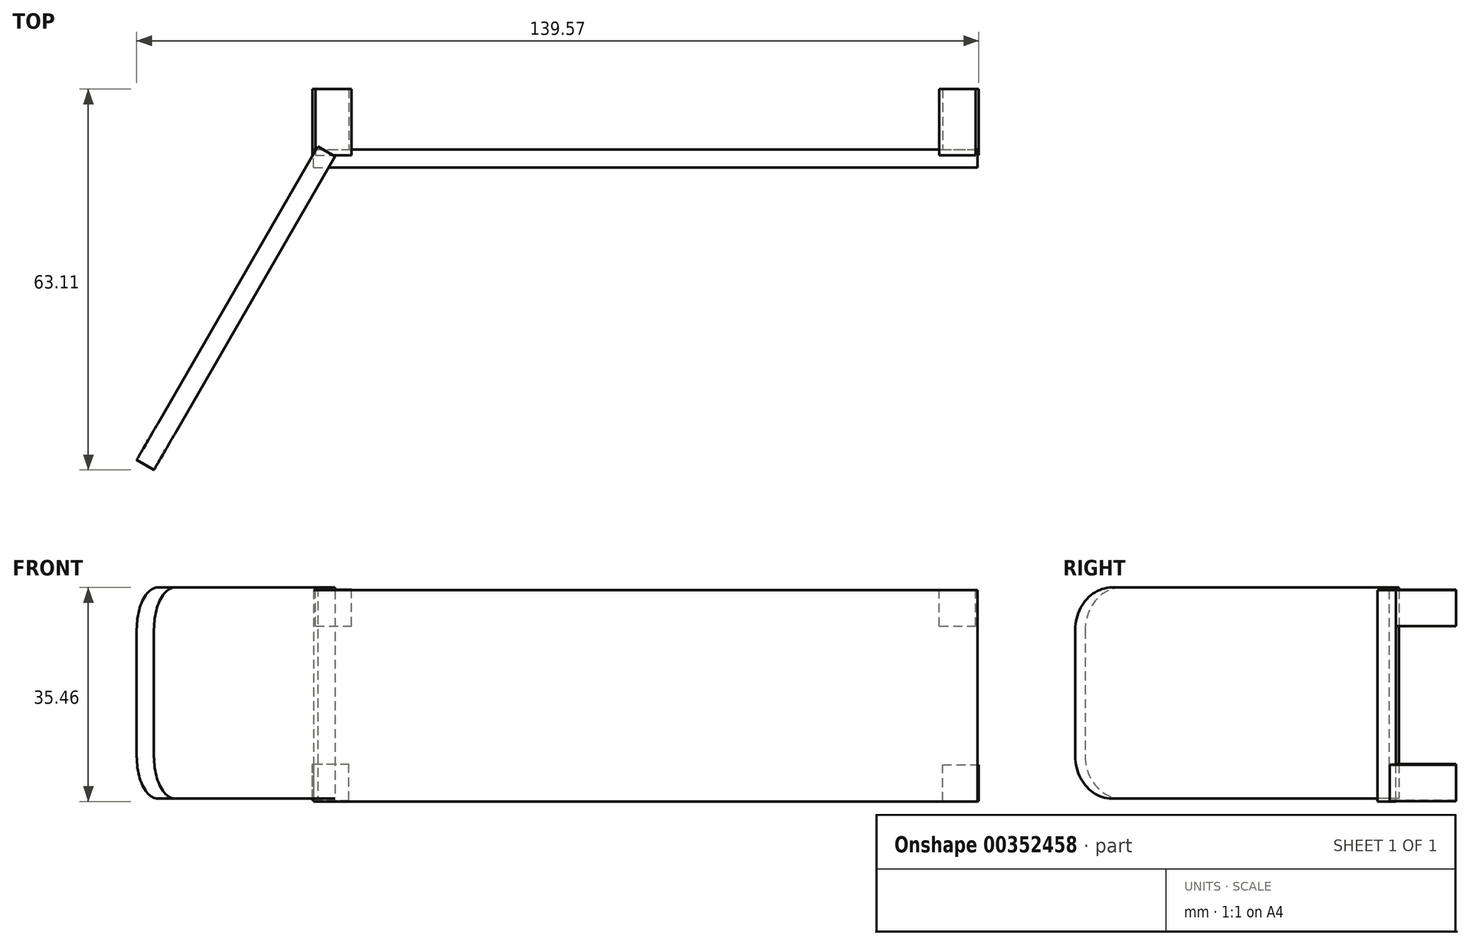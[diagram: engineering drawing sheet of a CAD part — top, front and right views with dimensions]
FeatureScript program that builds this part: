
annotation { "Feature Type Name" : "Feature", "Feature Type Description" : "" }
export const myFeature = defineFeature(function(context is Context, id is Id, definition is map)
    precondition{}
    {
        {
            var Q0;
            Q0=qCreatedBy(makeId("Front.planeOp"),FACE);
            var sketch = newSketch(context, id + "F0", { "sketchPlane" : qUnion([Q0])});
            skLineSegment(sketch, "E0.bottom", {"start": v(-50.03, 27.7) * mm, "end": v(59.97, 27.7) * mm});
            skLineSegment(sketch, "E0.top", {"start": v(-50.03, -7.3) * mm, "end": v(59.97, -7.3) * mm});
            skLineSegment(sketch, "E0.left", {"start": v(-50.03, 27.7) * mm, "end": v(-50.03, -7.3) * mm});
            skLineSegment(sketch, "E0.right", {"start": v(59.97, 27.7) * mm, "end": v(59.97, -7.3) * mm});
            skSolve(sketch);
        }
        {
            var Q0;
            Q0 = qSketchRegion(id + "F0", true);
            extrude(context, id + "F1", {"entities" : qUnion([Q0]), "depth" : 3 * mm});
        }
        {
            var Q0;
            Q0=qCreatedBy(makeId("Front.planeOp"),FACE);
            var sketch = newSketch(context, id + "F2", { "sketchPlane" : qUnion([Q0])});
            skLineSegment(sketch, "E1.bottom", {"start": v(-50.21, -7.14) * mm, "end": v(-44.21, -7.14) * mm});
            skLineSegment(sketch, "E1.top", {"start": v(-50.21, -1.14) * mm, "end": v(-44.21, -1.14) * mm});
            skLineSegment(sketch, "E1.left", {"start": v(-50.21, -7.14) * mm, "end": v(-50.21, -1.14) * mm});
            skLineSegment(sketch, "E1.right", {"start": v(-44.21, -7.14) * mm, "end": v(-44.21, -1.14) * mm});
            skLineSegment(sketch, "E2.bottom", {"start": v(-49.75, 21.78) * mm, "end": v(-43.75, 21.78) * mm});
            skLineSegment(sketch, "E2.top", {"start": v(-49.75, 27.78) * mm, "end": v(-43.75, 27.78) * mm});
            skLineSegment(sketch, "E2.left", {"start": v(-49.75, 21.78) * mm, "end": v(-49.75, 27.78) * mm});
            skLineSegment(sketch, "E2.right", {"start": v(-43.75, 21.78) * mm, "end": v(-43.75, 27.78) * mm});
            skLineSegment(sketch, "E3.bottom", {"start": v(54.2, -7.26) * mm, "end": v(60.2, -7.26) * mm});
            skLineSegment(sketch, "E3.top", {"start": v(54.2, -1.26) * mm, "end": v(60.2, -1.26) * mm});
            skLineSegment(sketch, "E3.left", {"start": v(54.2, -7.26) * mm, "end": v(54.2, -1.26) * mm});
            skLineSegment(sketch, "E3.right", {"start": v(60.2, -7.26) * mm, "end": v(60.2, -1.26) * mm});
            skLineSegment(sketch, "E4.bottom", {"start": v(53.68, 21.72) * mm, "end": v(59.68, 21.72) * mm});
            skLineSegment(sketch, "E4.top", {"start": v(53.68, 27.72) * mm, "end": v(59.68, 27.72) * mm});
            skLineSegment(sketch, "E4.left", {"start": v(53.68, 21.72) * mm, "end": v(53.68, 27.72) * mm});
            skLineSegment(sketch, "E4.right", {"start": v(59.68, 21.72) * mm, "end": v(59.68, 27.72) * mm});
            skSolve(sketch);
        }
        {
            var Q0;
            Q0 = qSketchRegion(id + "F2", true);
            extrude(context, id + "F3", {"entities" : qUnion([Q0]), "operationType" : NewBodyOperationType.ADD, "oppositeDirection" : true, "depth" : 10 * mm, "hasSecondDirection" : true, "secondDirectionOppositeDirection" : false, "secondDirectionDepth" : 1 * mm});
        }
        {
            var Q0;
            Q0=qCreatedBy(makeId("Right.planeOp"),FACE);
            var sketch = newSketch(context, id + "F4", { "sketchPlane" : qUnion([Q0])});
            skLineSegment(sketch, "E5.bottom", {"start": v(-1.15, 28.15) * mm, "end": v(-61.15, 28.15) * mm});
            skLineSegment(sketch, "E5.top", {"start": v(-1.15, -6.83) * mm, "end": v(-61.15, -6.83) * mm});
            skLineSegment(sketch, "E5.left", {"start": v(-1.15, 28.15) * mm, "end": v(-1.15, -6.83) * mm});
            skLineSegment(sketch, "E5.right", {"start": v(-61.15, 28.15) * mm, "end": v(-61.15, -6.83) * mm});
            skSolve(sketch);
        }
        {
            var Q0;
            Q0 = qSketchRegion(id + "F4", true);
            extrude(context, id + "F5", {"entities" : qUnion([Q0]), "oppositeDirection" : true, "depth" : 49.8 * mm, "hasSecondDirection" : true, "secondDirectionOppositeDirection" : true, "secondDirectionDepth" : 46.5 * mm});
        }
        {
            var Q0;
            Q0=makeQuery(id+"F5.opExtrude","SWEPT_EDGE",EDGE,{"disambiguationData":[OSD([sQuery(id+"F4.wireOp",EDGE,"E5.top"),sQuery(id+"F4.wireOp",EDGE,"E5.right")])]});
            var Q1;
            Q1=makeQuery(id+"F5.opExtrude","SWEPT_EDGE",EDGE,{"disambiguationData":[OSD([sQuery(id+"F4.wireOp",EDGE,"E5.bottom"),sQuery(id+"F4.wireOp",EDGE,"E5.right")])]});
            fillet(context, id + "F6", {"entities" : qUnion([Q0, Q1]), "radius" : 7 * mm, "tangentPropagation" : true, "allowEdgeOverflow" : false});
        }
        {
            var Q0;
            Q0=makeQuery(id+"F5.opExtrude","SWEPT_BODY",BODY,{"disambiguationData":[OSD([sQuery(id+"F4.wireOp",EDGE,"E5.bottom"),sQuery(id+"F4.wireOp",EDGE,"E5.top"),sQuery(id+"F4.wireOp",EDGE,"E5.left"),sQuery(id+"F4.wireOp",EDGE,"E5.right")])]});
            var Q1;
            Q1=makeQuery(id+"F5.opExtrude","CAP_EDGE",EDGE,{"disambiguationData":[OSD([sQuery(id+"F4.wireOp",EDGE,"E5.left")])],"isStart":true});
            transform(context, id + "F7", {"entities" : qUnion([Q0]), "transformType" : TransformType.ROTATION, "transformAxis" : qUnion([Q1]), "angle" : 30 * degree, "makeCopy" : false});
        }
    });
